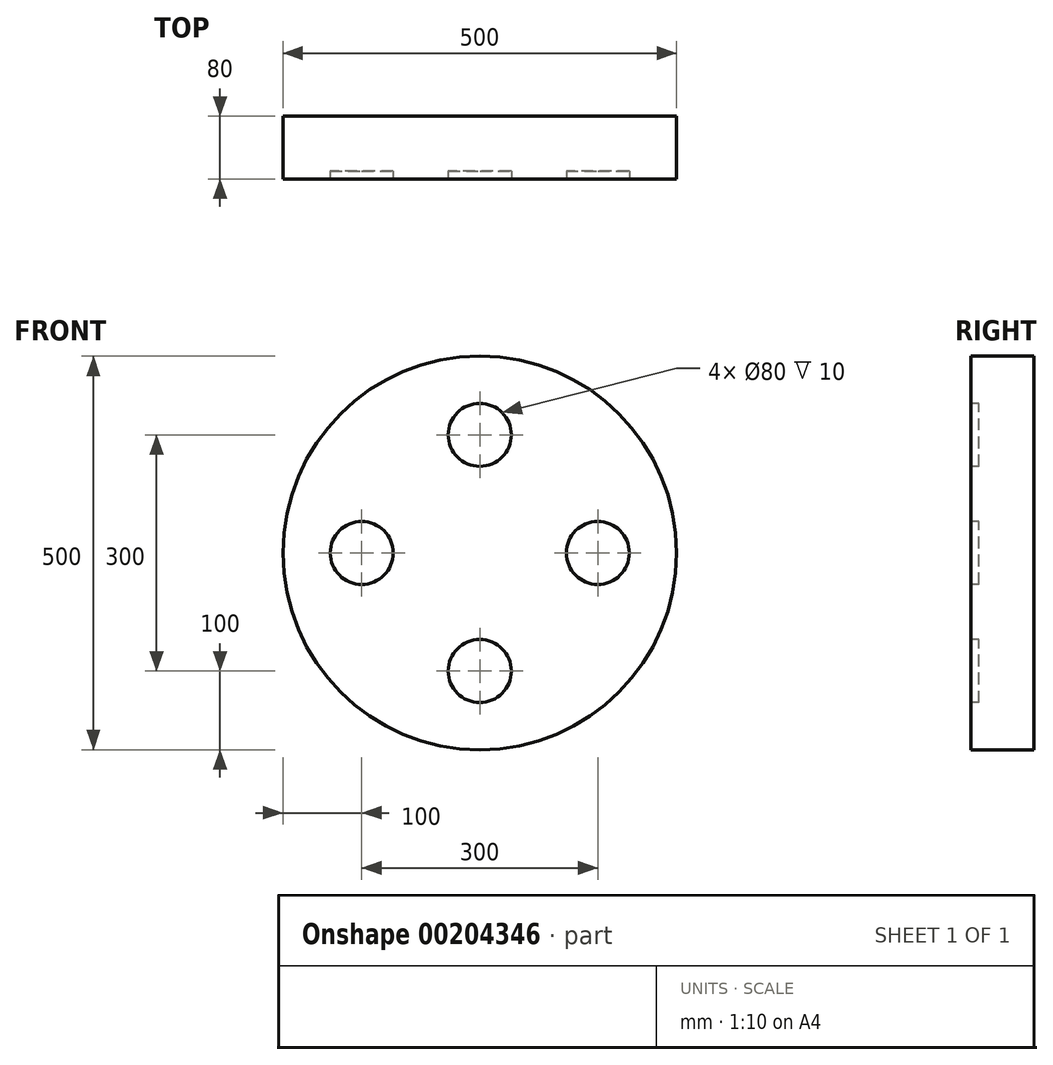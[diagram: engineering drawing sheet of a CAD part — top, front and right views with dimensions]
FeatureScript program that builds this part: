
annotation { "Feature Type Name" : "Feature", "Feature Type Description" : "" }
export const myFeature = defineFeature(function(context is Context, id is Id, definition is map)
    precondition{}
    {
        {
            var Q0;
            Q0=qCreatedBy(makeId("Front.planeOp"),FACE);
            var sketch = newSketch(context, id + "F0", { "sketchPlane" : qUnion([Q0])});
            skCircle(sketch, "E0", {"center": v(0, 0) * mm, "radius": 250 * mm});
            skSolve(sketch);
        }
        {
            var Q0;
            Q0 = qSketchRegion(id + "F0", true);
            extrude(context, id + "F1", {"entities" : qUnion([Q0]), "depth" : 80 * mm});
        }
        {
            var Q0;
            Q0=makeQuery(id+"F1.opExtrude","CAP_FACE",FACE,{"disambiguationData":[OSD([sQuery(id+"F0.wireOp",EDGE,"E0")])],"isStart":false});
            var sketch = newSketch(context, id + "F2", { "sketchPlane" : qUnion([Q0])});
            skCircle(sketch, "E1", {"center": v(0, 150) * mm, "radius": 40 * mm});
            skCircle(sketch, "E2.1.0", {"center": v(-150, 0) * mm, "radius": 40 * mm});
            skCircle(sketch, "E2.2.0", {"center": v(0, -150) * mm, "radius": 40 * mm});
            skCircle(sketch, "E2.3.0", {"center": v(150, 0) * mm, "radius": 40 * mm});
            skPoint(sketch, "E2.center", {"position": v(0, 0) * mm});
            skSolve(sketch);
        }
        {
            var Q0;
            Q0 = qSketchRegion(id + "F2", true);
            extrude(context, id + "F3", {"entities" : qUnion([Q0]), "operationType" : NewBodyOperationType.REMOVE, "oppositeDirection" : true, "depth" : 10 * mm});
        }
    });
